# Revit family: IS_Tesi_T5524_BIM_NL
name_source: partatom
category: Plumbing Fixtures
units: mm (PartAtom-declared; Revit-internal decimal feet)

## family parameters
Always vertical = No
Cut with Voids When Loaded = No
OmniClass Number = 23.45.05.21.11.11
OmniClass Title = Water Operated Water Closets
Part Type = Normal
Room Calculation Point = No
Round Connector Dimension = Use Diameter
Shared = No
Work Plane-Based = No

## types (3) — shared parameters
Afmetingen = 45 x 447 x 366 mm
AfstandsEenheid = Millimeter
Auteur = Ideal Standard
BIMobject category = Toilet Seats
BIMobject category code = toilet-seats
BIMobject main category = Sanitary
BIMobject main category code = sanitary
Beschrijvinggarantie = Herstellergarantie
BimObjectNaam = IS_IdealStandard_WCseatsandcovers_Tesi_T5524_IdealStandard
Brand url = https://www.idealstandard.nl
Breedte = 365.9681
Date of publishing = 15/03/2023
Diepte = 447 mm
DuurEenheid = Jahre
Edition number = 1
Garantieonderdelen = https://www.idealstandard.nl
Garantieunits = Jahre
GemaaktOp = 15/03/2023
Hoogte = 44,7218539552065
Hulp = https://www.idealstandard.nl
IFC Classification = Sanitary Terminal
IfcExportAs = IfcSanitaryTerminalType
IfcExportType = WCSEAT
Installatieinstructies = https://www.idealstandard.nl
Installation instructions = https://www.idealstandard.nl
Lengte = 447 mm
Manufacturer = Ideal Standard
Manufacturer name = Ideal Standard
Masterformat 2014 Code = 10 28 13
Masterformat 2014 Description = Toilet Accessories
Materiaal = Duroplast
MateriaalWC = Duroplast
Material main = Duroplast
Merk = Ideal Standard
Montageinstuctie = https://www.idealstandard.nl
NBS Reference Code = 45-35-70/391
NBS Reference Description = WC seats and covers
Nettogewicht = 2.08
NominalHeight = 45 mm
NominalLength = 447 mm
NominalWidth = 366 mm
OmniClass Code = 23-31 19 19 17
OmniClass Description = Water Closet Seats
OppervlakteEenheid = Millimeter
Product Guid = 0a2043a8-8fa7-4624-9c92-985bd69c0c84
Product SKU = T5524
Product certification = https://www.idealstandard.nl
Product data url = https://bimobject.com
Product family = TESI
Product group = Tesi
Product name = TESI S&C WO SC TO FOR EASYFIX
Product url = https://www.idealstandard.nl
Productinformatie = https://www.idealstandard.nl
QR code = http://bimobject.com
Revisie = 1
Size = 45 x 447 x 366 mm
Technical description = https://www.idealstandard.nl
Telefoonnummer = 077 355 08 08
Toepassing = WC Seat & Cover
Typeconnectie = Installation
UNSPSC Code = 301815
URL = https://www.idealstandard.nl
Uniclass 2015 Code = Pr_40_20_93_95
Uniclass 2015 Name = WC seats and covers
Uniclass2015Beschrijving = WC seats and covers
Uniclass2015Referentie = Pr_40_20_93_95
Uniclass2015Version = v1.26
Uniformat II Code = D2010
Uniformat II Description = Plumbing Fixtures
Urlproducent = https://www.idealstandard.nl
ValutaEenheid = Euro
Versie = 1
Verwachtelevensduur = 5
Volumeunits = Liter
Vorm = geformt
Wisselstukken = https://www.idealstandard.nl
Youtube clip = https://www.youtube.com
zero-valued in all types: BrutoGewicht, Cost, Default Elevation, Vervangingskosten

## per-type parameters (varying)
| type | Afwerking | Artikelnummer | Artikelomschrijving | Artikelreferentie | Barcode | Description | Eigenschappen | GTIN code | Kleur | Model | Referentie |
| T552401 - Tesi seat & cover soft close close, wraopver, Quick release for EASY FIX+ bowl, in white | Weiß | T552401 | Ideal Standard Tesi Sitz und Deckel mit Soft-Close-Funktion, Wrapover, Schnelllösefunktion für EASY FIX+ Schüssel, in Weiß. | T552401 | 8014140515135 | Tesi Sitz und Deckel mit Soft-Close-Funktion, Wrapover, Schnelllösefunktion für EASY FIX+ Schüssel, in Weiß. | Sitz und Deckel mit Soft-Close-Funktion, Wrapover, Schnelllösefunktion für EASY FIX+ Schüssel, in Weiß. | 8014140515135 | Weiß | T552401 | Ideal Standard Tesi Sitz und Deckel mit Soft-Close-Funktion, Wrapover, Schnelllösefunktion für EASY FIX+ Schüssel, in Weiß. |
| T5524V1 - Tesi seat & cover soft close close, wraopver, Quick release for EASY FIX+ bowl, in SILK WHITE | Seidenweiß | T5524V1 | Ideal Standard Tesi Sitz und Deckel mit Soft-Close-Funktion, Wrapover, Schnelllösefunktion für EASY FIX+ Schüssel, in Seidenschwarz | T5524V1 | 8014140515142 | Tesi Sitz und Deckel mit Soft-Close-Funktion, Wrapover, Schnelllösefunktion für EASY FIX+ Schüssel, in Seidenschwarz | Sitz und Deckel mit Soft-Close-Funktion, Wrapover, Schnelllösefunktion für EASY FIX+ Schüssel, in Seidenschwarz | 8014140515142 | Seidenweiß | T5524V1 | Ideal Standard Tesi Sitz und Deckel mit Soft-Close-Funktion, Wrapover, Schnelllösefunktion für EASY FIX+ Schüssel, in Seidenschwarz |
| T5524V3 - Tesi seat & cover soft close close, wraopver, Quick release for EASY FIX+ bowl, in SILK BLACK | Seidenschwarz | T5524V3 | Ideal Standard Tesi Sitz und Deckel mit Soft-Close-Funktion, Wrapover, Schnelllösefunktion für EASY FIX+ Schüssel, in Seidenschwarz | T5524V3 | 8014140515159 | Tesi Sitz und Deckel mit Soft-Close-Funktion, Wrapover, Schnelllösefunktion für EASY FIX+ Schüssel, in Seidenschwarz | Sitz und Deckel mit Soft-Close-Funktion, Wrapover, Schnelllösefunktion für EASY FIX+ Schüssel, in Seidenschwarz | 8014140515159 | Seidenschwarz | T5524V3 | Ideal Standard Tesi Sitz und Deckel mit Soft-Close-Funktion, Wrapover, Schnelllösefunktion für EASY FIX+ Schüssel, in Seidenschwarz |

## geometry (parser evidence)
native form markers: Blend x4, Sweep x3
no freeform markers — native parametric forms only
